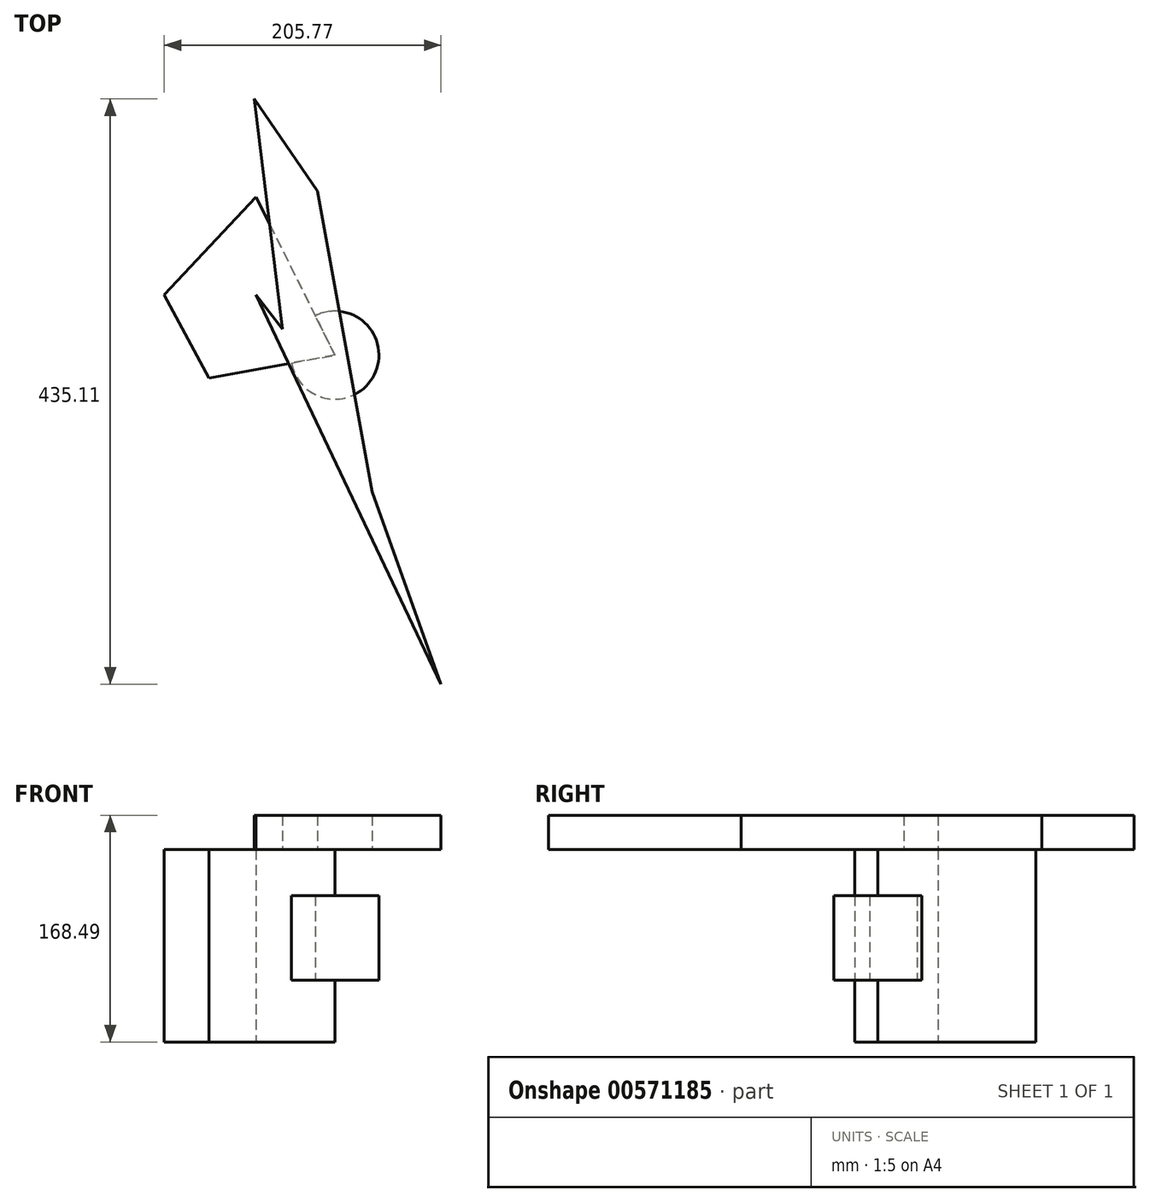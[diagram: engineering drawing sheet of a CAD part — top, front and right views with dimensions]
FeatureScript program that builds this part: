
annotation { "Feature Type Name" : "Feature", "Feature Type Description" : "" }
export const myFeature = defineFeature(function(context is Context, id is Id, definition is map)
    precondition{}
    {
        {
            var Q0;
            Q0=qCreatedBy(makeId("Top.planeOp"),FACE);
            var sketch = newSketch(context, id + "F0", { "sketchPlane" : qUnion([Q0])});
            skLineSegment(sketch, "E0", {"start": v(0, 0) * mm, "end": v(68.23, 72.85) * mm});
            skLineSegment(sketch, "E1", {"start": v(68.23, 72.85) * mm, "end": v(126.88, -44.8) * mm});
            skLineSegment(sketch, "E2", {"start": v(126.88, -44.8) * mm, "end": v(33.12, -61.83) * mm});
            skLineSegment(sketch, "E3", {"start": v(33.12, -61.83) * mm, "end": v(0, 0) * mm});
            skSolve(sketch);
        }
        {
            var Q0;
            Q0=makeQuery(id+"F0.imprint","IMPRINT",FACE,{"disambiguationData":[TD([[makeQuery(id+"F0.imprint","IMPRINT",EDGE,{"derivedFrom":sQuery(id+"F0.wireOp",EDGE,"E0")}),-1.0]])]});
            extrude(context, id + "F1", {"entities" : qUnion([Q0]), "depth" : 143.1 * mm, "offsetDistance" : 25.4 * mm});
        }
        {
            var Q0;
            Q0=makeQuery(id+"F1.opExtrude","SWEPT_FACE",FACE,{"disambiguationData":[OSD([sQuery(id+"F0.wireOp",EDGE,"E2")])]});
            var sketch = newSketch(context, id + "F2", { "sketchPlane" : qUnion([Q0])});
            skLineSegment(sketch, "E4.bottom", {"start": v(116.83, 45.98) * mm, "end": v(149.55, 45.98) * mm});
            skLineSegment(sketch, "E4.top", {"start": v(116.83, 108.78) * mm, "end": v(149.55, 108.78) * mm});
            skLineSegment(sketch, "E4.left", {"start": v(116.83, 45.98) * mm, "end": v(116.83, 108.78) * mm});
            skLineSegment(sketch, "E4.right", {"start": v(149.55, 45.98) * mm, "end": v(149.55, 108.78) * mm});
            skSolve(sketch);
        }
        {
            var Q0;
            Q0=makeQuery(id+"F2.imprint","IMPRINT",FACE,{"disambiguationData":[TD([[makeQuery(id+"F2.imprint","IMPRINT",EDGE,{"derivedFrom":sQuery(id+"F2.wireOp",EDGE,"E4.bottom")}),1.0]])]});
            var Q1;
            Q1=sQuery(id+"F2.wireOp",EDGE,"E4.left");
            revolve(context, id + "F3", {"operationType" : NewBodyOperationType.ADD, "entities" : qUnion([Q0]), "axis" : qUnion([Q1]), "revolveType" : RevolveType.FULL});
        }
        {
            var Q0;
            Q0=makeQuery(id+"F1.opExtrude","CAP_FACE",FACE,{"disambiguationData":[OSD([sQuery(id+"F0.wireOp",EDGE,"E0"),sQuery(id+"F0.wireOp",EDGE,"E1"),sQuery(id+"F0.wireOp",EDGE,"E2"),sQuery(id+"F0.wireOp",EDGE,"E3")])],"isStart":false});
            var sketch = newSketch(context, id + "F4", { "sketchPlane" : qUnion([Q0])});
            skLineSegment(sketch, "E5", {"start": v(68.23, 0) * mm, "end": v(87.74, -25.42) * mm});
            skLineSegment(sketch, "E6", {"start": v(87.74, -25.42) * mm, "end": v(67.02, 145.65) * mm});
            skLineSegment(sketch, "E7", {"start": v(67.02, 145.65) * mm, "end": v(113.96, 77.19) * mm});
            skLineSegment(sketch, "E8", {"start": v(113.96, 77.19) * mm, "end": v(154.56, -146.41) * mm});
            skLineSegment(sketch, "E9", {"start": v(154.56, -146.41) * mm, "end": v(205.77, -289.46) * mm});
            skLineSegment(sketch, "E10", {"start": v(205.77, -289.46) * mm, "end": v(68.23, 0) * mm});
            skSolve(sketch);
        }
        {
            var Q0;
            {var subQ1=sQuery(id+"F4.wireOp",EDGE,"E7");Q0=makeQuery(id+"F4.imprint","IMPRINT",FACE,{"disambiguationData":[TD([[makeQuery(id+"F4.imprint","IMPRINT",EDGE,{"derivedFrom":subQ1}),-1.0]])]});}
            var Q1;
            {var subQ1=sQuery(id+"F4.wireOp",EDGE,"E5");Q1=makeQuery(id+"F4.imprint","IMPRINT",FACE,{"disambiguationData":[TD([[makeQuery(id+"F4.imprint","IMPRINT",EDGE,{"derivedFrom":subQ1}),-1.0]])]});}
            extrude(context, id + "F5", {"entities" : qUnion([Q0, Q1]), "operationType" : NewBodyOperationType.ADD, "depth" : 25.4 * mm, "offsetDistance" : 25.4 * mm});
        }
    });
